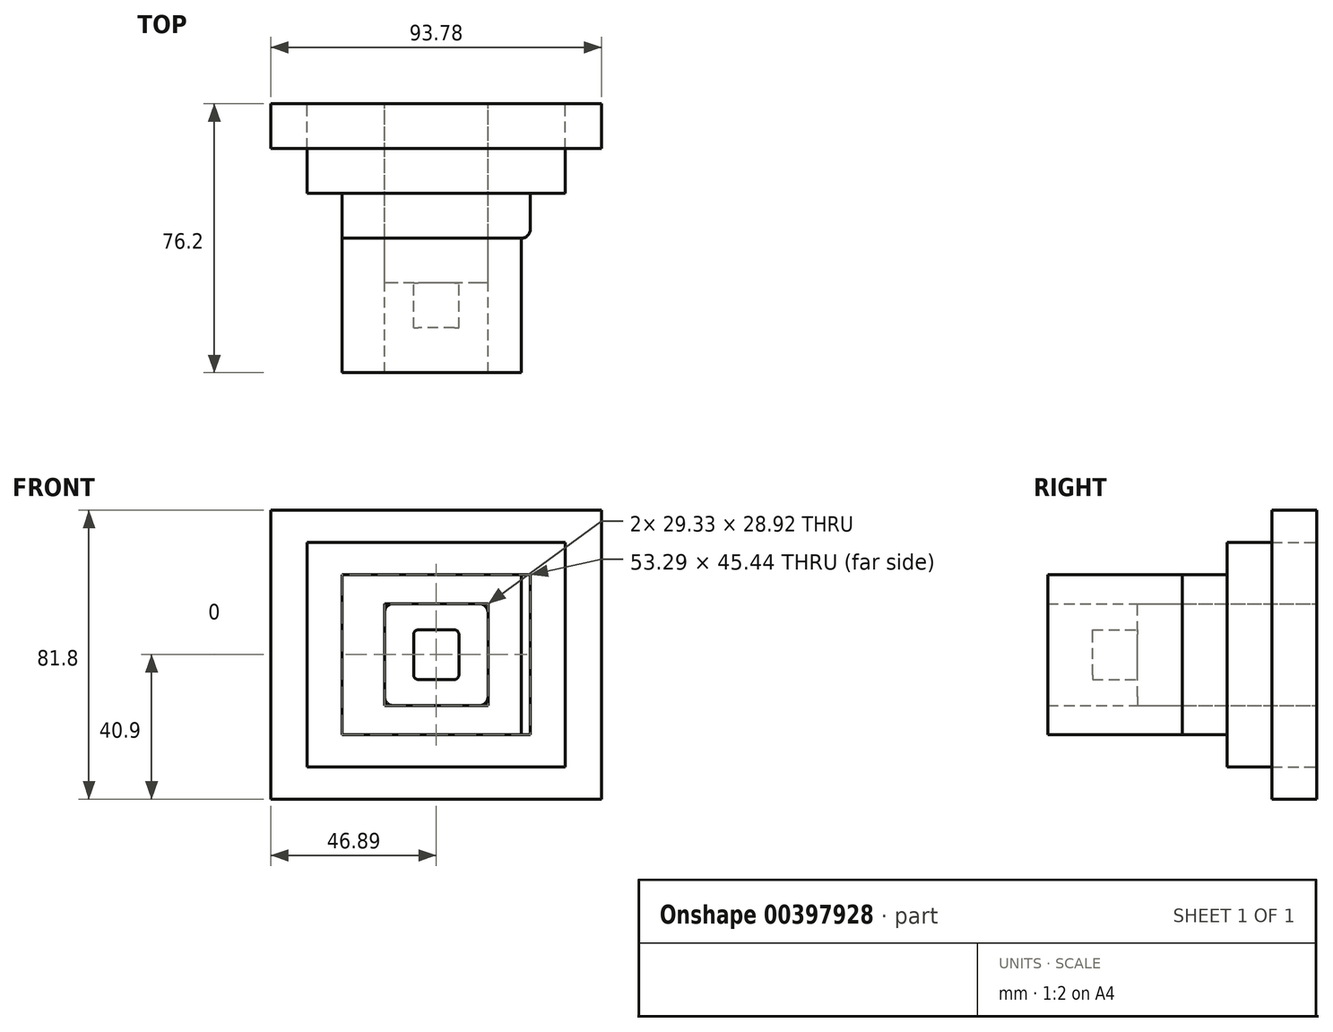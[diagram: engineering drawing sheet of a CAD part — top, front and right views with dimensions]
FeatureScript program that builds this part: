
annotation { "Feature Type Name" : "Feature", "Feature Type Description" : "" }
export const myFeature = defineFeature(function(context is Context, id is Id, definition is map)
    precondition{}
    {
        {
            var Q0;
            Q0=qCreatedBy(makeId("Front.planeOp"),FACE);
            var sketch = newSketch(context, id + "F0", { "sketchPlane" : qUnion([Q0])});
            skLineSegment(sketch, "E0.bottom", {"start": v(6.4, -7.02) * mm, "end": v(-6.4, -7.02) * mm});
            skLineSegment(sketch, "E0.top", {"start": v(6.4, 7.02) * mm, "end": v(-6.4, 7.02) * mm});
            skLineSegment(sketch, "E0.left", {"start": v(6.4, -7.02) * mm, "end": v(6.4, 7.02) * mm});
            skLineSegment(sketch, "E0.right", {"start": v(-6.4, -7.02) * mm, "end": v(-6.4, 7.02) * mm});
            skPoint(sketch, "E0.middle", {"position": v(0, 0) * mm});
            skLineSegment(sketch, "E1.bottom", {"start": v(14.67, -14.46) * mm, "end": v(-14.67, -14.46) * mm});
            skLineSegment(sketch, "E1.top", {"start": v(14.67, 14.46) * mm, "end": v(-14.67, 14.46) * mm});
            skLineSegment(sketch, "E1.left", {"start": v(14.67, -14.46) * mm, "end": v(14.67, 14.46) * mm});
            skLineSegment(sketch, "E1.right", {"start": v(-14.67, -14.46) * mm, "end": v(-14.67, 14.46) * mm});
            skLineSegment(sketch, "E2.bottom", {"start": v(26.65, -22.72) * mm, "end": v(-26.65, -22.72) * mm});
            skLineSegment(sketch, "E2.top", {"start": v(26.65, 22.72) * mm, "end": v(-26.65, 22.72) * mm});
            skLineSegment(sketch, "E2.left", {"start": v(26.65, -22.72) * mm, "end": v(26.65, 22.72) * mm});
            skLineSegment(sketch, "E2.right", {"start": v(-26.65, -22.72) * mm, "end": v(-26.65, 22.72) * mm});
            skLineSegment(sketch, "E3.bottom", {"start": v(36.56, -31.81) * mm, "end": v(-36.56, -31.81) * mm});
            skLineSegment(sketch, "E3.top", {"start": v(36.56, 31.81) * mm, "end": v(-36.56, 31.81) * mm});
            skLineSegment(sketch, "E3.left", {"start": v(36.56, -31.81) * mm, "end": v(36.56, 31.81) * mm});
            skLineSegment(sketch, "E3.right", {"start": v(-36.56, -31.81) * mm, "end": v(-36.56, 31.81) * mm});
            skLineSegment(sketch, "E4.bottom", {"start": v(46.9, -40.9) * mm, "end": v(-46.9, -40.9) * mm});
            skLineSegment(sketch, "E4.top", {"start": v(46.9, 40.9) * mm, "end": v(-46.9, 40.9) * mm});
            skLineSegment(sketch, "E4.left", {"start": v(46.9, -40.9) * mm, "end": v(46.9, 40.9) * mm});
            skLineSegment(sketch, "E4.right", {"start": v(-46.9, -40.9) * mm, "end": v(-46.9, 40.9) * mm});
            skSolve(sketch);
        }
        {
            var Q0;
            Q0=makeQuery(id+"F0.imprint","IMPRINT",FACE,{"disambiguationData":[TD([[makeQuery(id+"F0.imprint","IMPRINT",EDGE,{"derivedFrom":sQuery(id+"F0.wireOp",EDGE,"E3.bottom")}),1.0]])]});
            extrude(context, id + "F1", {"entities" : qUnion([Q0]), "depth" : 12.7 * mm});
        }
        {
            var Q0;
            Q0=makeQuery(id+"F0.imprint","IMPRINT",FACE,{"disambiguationData":[TD([[makeQuery(id+"F0.imprint","IMPRINT",EDGE,{"derivedFrom":sQuery(id+"F0.wireOp",EDGE,"E1.bottom")}),1.0]])]});
            extrude(context, id + "F2", {"entities" : qUnion([Q0]), "operationType" : NewBodyOperationType.ADD, "depth" : 38.1 * mm});
        }
        {
            var Q0;
            Q0=makeQuery(id+"F0.imprint","IMPRINT",FACE,{"disambiguationData":[TD([[makeQuery(id+"F0.imprint","IMPRINT",EDGE,{"derivedFrom":sQuery(id+"F0.wireOp",EDGE,"E2.bottom")}),1.0]])]});
            extrude(context, id + "F3", {"entities" : qUnion([Q0]), "operationType" : NewBodyOperationType.ADD, "depth" : 25.4 * mm});
        }
        {
            var Q0;
            Q0=makeQuery(id+"F0.imprint","IMPRINT",FACE,{"disambiguationData":[TD([[makeQuery(id+"F0.imprint","IMPRINT",EDGE,{"derivedFrom":sQuery(id+"F0.wireOp",EDGE,"E2.bottom")}),1.0]])]});
            extrude(context, id + "F4", {"entities" : qUnion([Q0]), "depth" : 25.4 * mm});
        }
        {
            var Q0;
            Q0=makeQuery(id+"F0.imprint","IMPRINT",FACE,{"disambiguationData":[TD([[makeQuery(id+"F0.imprint","IMPRINT",EDGE,{"derivedFrom":sQuery(id+"F0.wireOp",EDGE,"E0.bottom")}),1.0]])]});
            extrude(context, id + "F5", {"entities" : qUnion([Q0]), "depth" : 50.8 * mm});
        }
        {
            var Q0;
            Q0=makeQuery(id+"F0.imprint","IMPRINT",FACE,{"disambiguationData":[TD([[makeQuery(id+"F0.imprint","IMPRINT",EDGE,{"derivedFrom":sQuery(id+"F0.wireOp",EDGE,"E0.bottom")}),-1.0]])]});
            extrude(context, id + "F6", {"entities" : qUnion([Q0]), "operationType" : NewBodyOperationType.ADD, "depth" : 63.5 * mm});
        }
        {
            var Q0;
            Q0=makeQuery(id+"F6.opExtrude","SWEPT_EDGE",EDGE,{"disambiguationData":[OSD([sQuery(id+"F0.wireOp",EDGE,"E0.top"),sQuery(id+"F0.wireOp",EDGE,"E0.left")])]});
            var Q1;
            Q1=makeQuery(id+"F6.opExtrude","SWEPT_EDGE",EDGE,{"disambiguationData":[OSD([sQuery(id+"F0.wireOp",EDGE,"E0.bottom"),sQuery(id+"F0.wireOp",EDGE,"E0.left")])]});
            var Q2;
            Q2=makeQuery(id+"F6.opExtrude","SWEPT_EDGE",EDGE,{"disambiguationData":[OSD([sQuery(id+"F0.wireOp",EDGE,"E0.top"),sQuery(id+"F0.wireOp",EDGE,"E0.right")])]});
            var Q3;
            Q3=makeQuery(id+"F6.opExtrude","SWEPT_EDGE",EDGE,{"disambiguationData":[OSD([sQuery(id+"F0.wireOp",EDGE,"E0.bottom"),sQuery(id+"F0.wireOp",EDGE,"E0.right")])]});
            fillet(context, id + "F7", {"entities" : qUnion([Q0, Q1, Q2, Q3]), "radius" : 1.27 * mm, "tangentPropagation" : true, "allowEdgeOverflow" : false});
        }
        {
            var Q0;
            Q0=makeQuery(id+"F2.opExtrude","CAP_EDGE",EDGE,{"disambiguationData":[OSD([sQuery(id+"F0.wireOp",EDGE,"E2.left")])],"isStart":false});
            var Q1;
            Q1=makeQuery(id+"F5.opExtrude","SWEPT_EDGE",EDGE,{"disambiguationData":[OSD([sQuery(id+"F0.wireOp",EDGE,"E1.bottom"),sQuery(id+"F0.wireOp",EDGE,"E1.left")])]});
            var Q2;
            Q2=makeQuery(id+"F5.opExtrude","SWEPT_EDGE",EDGE,{"disambiguationData":[OSD([sQuery(id+"F0.wireOp",EDGE,"E1.bottom"),sQuery(id+"F0.wireOp",EDGE,"E1.right")])]});
            var Q3;
            Q3=makeQuery(id+"F5.opExtrude","SWEPT_EDGE",EDGE,{"disambiguationData":[OSD([sQuery(id+"F0.wireOp",EDGE,"E1.top"),sQuery(id+"F0.wireOp",EDGE,"E1.right")])]});
            var Q4;
            Q4=makeQuery(id+"F5.opExtrude","SWEPT_EDGE",EDGE,{"disambiguationData":[OSD([sQuery(id+"F0.wireOp",EDGE,"E1.top"),sQuery(id+"F0.wireOp",EDGE,"E1.left")])]});
            fillet(context, id + "F8", {"entities" : qUnion([Q0, Q1, Q2, Q3, Q4]), "radius" : 2.54 * mm, "tangentPropagation" : true, "allowEdgeOverflow" : false});
        }
        {
            var Q0;
            Q0=makeQuery(id+"F2.opExtrude","CAP_FACE",FACE,{"disambiguationData":[OSD([sQuery(id+"F0.wireOp",EDGE,"E1.bottom"),sQuery(id+"F0.wireOp",EDGE,"E1.top"),sQuery(id+"F0.wireOp",EDGE,"E1.left"),sQuery(id+"F0.wireOp",EDGE,"E1.right"),sQuery(id+"F0.wireOp",EDGE,"E2.bottom"),sQuery(id+"F0.wireOp",EDGE,"E2.top"),sQuery(id+"F0.wireOp",EDGE,"E2.left"),sQuery(id+"F0.wireOp",EDGE,"E2.right")])],"isStart":false});
            extrude(context, id + "F9", {"entities" : qUnion([Q0]), "depth" : 38.1 * mm});
        }
    });
